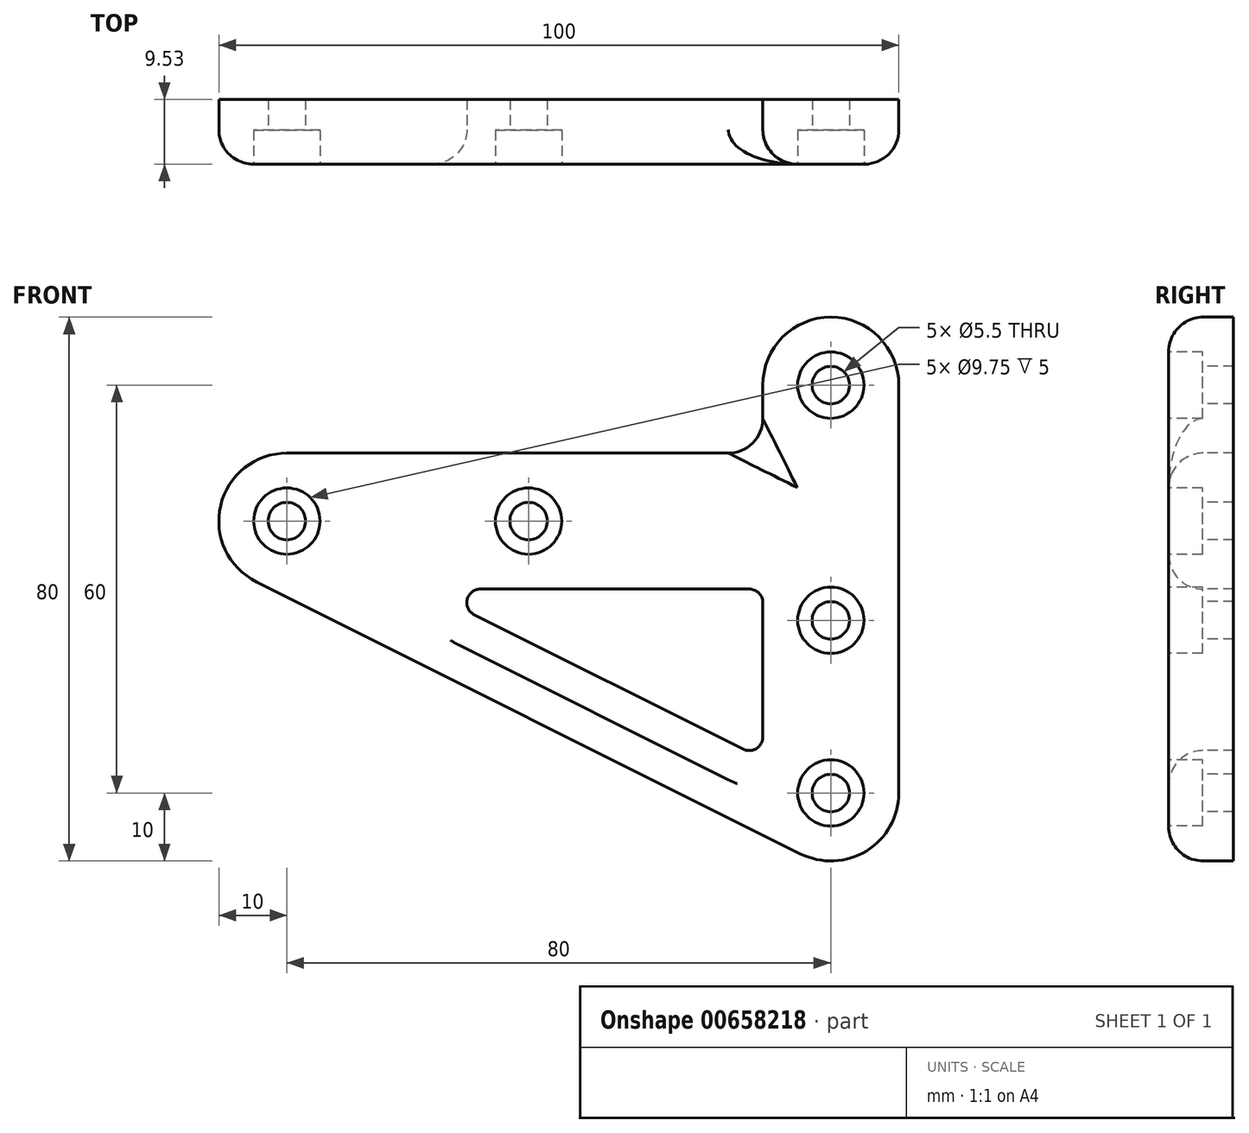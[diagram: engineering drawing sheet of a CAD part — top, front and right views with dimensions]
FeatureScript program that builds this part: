
annotation { "Feature Type Name" : "Feature", "Feature Type Description" : "" }
export const myFeature = defineFeature(function(context is Context, id is Id, definition is map)
    precondition{}
    {
        {
            var Q0;
            Q0=qCreatedBy(makeId("Front.planeOp"),FACE);
            var sketch = newSketch(context, id + "F0", { "sketchPlane" : qUnion([Q0])});
            skPoint(sketch, "E0.MirrorP", {"position": v(-44.45, 0) * mm});
            skPoint(sketch, "E1", {"position": v(0, -40) * mm});
            skArc(sketch, "E2", {"start": v(-4.47, -48.94) * mm, "mid": v(5.26, -48.5) * mm, "end": v(10, -40) * mm});
            skArc(sketch, "E3", {"start": v(-80, 10) * mm, "mid": v(-89.73, 2.3) * mm, "end": v(-84.47, -8.94) * mm});
            skPoint(sketch, "E4", {"position": v(0, 0) * mm});
            skLineSegment(sketch, "E5", {"start": v(-84.47, -8.94) * mm, "end": v(-4.47, -48.94) * mm});
            skLineSegment(sketch, "E6", {"start": v(-80, 10) * mm, "end": v(-10, 10) * mm});
            skLineSegment(sketch, "E7", {"start": v(10, -40) * mm, "end": v(10, 0) * mm});
            skLineSegment(sketch, "E8.0", {"start": v(-52.42, -13.79) * mm, "end": v(-12.9, -33.55) * mm});
            skLineSegment(sketch, "E9.0", {"start": v(-10, -31.76) * mm, "end": v(-10, -12) * mm});
            skLineSegment(sketch, "E10.0", {"start": v(-51.53, -10) * mm, "end": v(-12, -10) * mm});
            skPoint(sketch, "E11.visualSharp", {"position": v(-60, -10) * mm});
            skArc(sketch, "E11.filletArc", {"start": v(-51.53, -10) * mm, "mid": v(-53.47, -11.54) * mm, "end": v(-52.42, -13.79) * mm});
            skPoint(sketch, "E12.visualSharp", {"position": v(-10, -10) * mm});
            skArc(sketch, "E12.filletArc", {"start": v(-10, -12) * mm, "mid": v(-10.59, -10.59) * mm, "end": v(-12, -10) * mm});
            skPoint(sketch, "E13.visualSharp", {"position": v(-10, -35) * mm});
            skArc(sketch, "E13.filletArc", {"start": v(-12.9, -33.55) * mm, "mid": v(-10.95, -33.47) * mm, "end": v(-10, -31.76) * mm});
            skPoint(sketch, "E14", {"position": v(0, 20) * mm});
            skArc(sketch, "E15", {"start": v(10, 20) * mm, "mid": v(0, 30) * mm, "end": v(-10, 20) * mm});
            skLineSegment(sketch, "E16", {"start": v(10, 0) * mm, "end": v(10, 20) * mm});
            skLineSegment(sketch, "E17", {"start": v(-10, 20) * mm, "end": v(-10, 10) * mm});
            skPoint(sketch, "E18", {"position": v(0, -14.6) * mm});
            skSolve(sketch);
        }
        {
            var Q0;
            Q0 = qSketchRegion(id + "F0", true);
            extrude(context, id + "F1", {"entities" : qUnion([Q0]), "oppositeDirection" : true, "depth" : 9.52 * mm, "offsetDistance" : 25.4 * mm});
        }
        {
            var Q0;
            Q0=sQuery(id+"F0.wireOp",VERTEX,"zsvrEA9L-wWyx-hmEm-44rT-VdmW2u0hRzRj.center");
            var Q1;
            Q1=sQuery(id+"F0.wireOp",VERTEX,"E1");
            var Q2;
            Q2=sQuery(id+"F0.wireOp",VERTEX,"E0.MirrorP");
            var Q3;
            Q3=sQuery(id+"F0.wireOp",VERTEX,"E3.center");
            var Q4;
            Q4=sQuery(id+"F0.wireOp",VERTEX,"E18");
            var Q5;
            Q5=sQuery(id+"F0.wireOp",VERTEX,"E14");
            var Q6;
            Q6=makeQuery(id+"F1.opExtrude","SWEPT_BODY",BODY,{"disambiguationData":[OSD([sQuery(id+"F0.wireOp",EDGE,"bf2f238d-4e1d-4e86-ab75-1465cd813df2.MirrorCS"),sQuery(id+"F0.wireOp",EDGE,"7d5bedbb-471c-4160-8e68-eb1f4d767648.MirrorCS"),sQuery(id+"F0.wireOp",EDGE,"bc7fee83-9e46-4c51-805a-8ae9689402aa.MirrorCS"),sQuery(id+"F0.wireOp",EDGE,"e5d497b7-cccf-4703-a1dc-18e520bbeae9.MirrorCS"),sQuery(id+"F0.wireOp",EDGE,"c155fd9a-5cc5-4759-a1c6-071fd15af197.MirrorCS"),sQuery(id+"F0.wireOp",EDGE,"33a989d6-5cc4-4172-ab73-ca817da9f412.MirrorCS"),sQuery(id+"F0.wireOp",EDGE,"1c3aec17-fec7-453e-8acd-3df81b9bc4e3.MirrorCS"),sQuery(id+"F0.wireOp",EDGE,"0cd19f4d-6d86-4b4a-a093-bb589b475590.MirrorCS"),sQuery(id+"F0.wireOp",EDGE,"eee5d6f5-912f-4719-99ba-1d72e724f1e9.MirrorCS"),sQuery(id+"F0.wireOp",EDGE,"64a401ff-d109-42b1-96b9-6f7f2e519c4d.MirrorCS"),sQuery(id+"F0.wireOp",EDGE,"2bc110f3-ae92-45de-b2b7-7df43831b8ab"),sQuery(id+"F0.wireOp",EDGE,"pibmvETk-c1Xj-BIgN-8uma-1jo4IxxjolSW")])]});
            var Q7;
            Q7=makeQuery(id+"F1.opExtrude","SWEPT_BODY",BODY,{"disambiguationData":[OSD([sQuery(id+"F0.wireOp",EDGE,"zsvrEA9L-wWyx-hmEm-44rT-VdmW2u0hRzRj"),sQuery(id+"F0.wireOp",EDGE,"E2"),sQuery(id+"F0.wireOp",EDGE,"E3"),sQuery(id+"F0.wireOp",EDGE,"E5"),sQuery(id+"F0.wireOp",EDGE,"E6"),sQuery(id+"F0.wireOp",EDGE,"E7"),sQuery(id+"F0.wireOp",EDGE,"E8.0"),sQuery(id+"F0.wireOp",EDGE,"E9.0"),sQuery(id+"F0.wireOp",EDGE,"E10.0"),sQuery(id+"F0.wireOp",EDGE,"E11.filletArc"),sQuery(id+"F0.wireOp",EDGE,"E12.filletArc"),sQuery(id+"F0.wireOp",EDGE,"E13.filletArc")])]});
            hole(context, id + "F2", {"style" : HoleStyle.C_BORE, "endStyle" : HoleEndStyle.THROUGH, "standardTappedOrClearance" : lookupTablePath({ "standard" : "ISO", "fit" : "Normal", "size" : "M5", "type" : "Clearance" }), "standardBlindInLast" : lookupTablePath({ "fit" : "Standard", "standard" : "ISO", "size" : "M5", "type" : "Clearance" }), "holeDiameter" : 5.5 * mm, "cBoreDiameter" : 9.75 * mm, "cBoreDepth" : 5 * mm, "majorDiameter" : 6.35 * mm, "isTappedThrough" : true, "tappedDepth" : 12.7 * mm, "tapClearance" : 3, "locations" : qUnion([Q0, Q1, Q2, Q3, Q4, Q5]), "scope" : qUnion([Q6, Q7])});
        }
        {
            var Q0;
            Q0=makeQuery(id+"F1.opExtrude","CAP_EDGE",EDGE,{"disambiguationData":[OSD([sQuery(id+"F0.wireOp",EDGE,"E6")])],"isStart":true});
            var Q1;
            Q1=makeQuery(id+"F1.opExtrude","CAP_EDGE",EDGE,{"disambiguationData":[OSD([sQuery(id+"F0.wireOp",EDGE,"E10.0")])],"isStart":true});
            fillet(context, id + "F3", {"entities" : qUnion([Q0, Q1]), "radius" : 5.08 * mm, "tangentPropagation" : true, "allowEdgeOverflow" : false});
        }
        {
            var Q0;
            Q0=makeQuery(id+"F1.opExtrude","SWEPT_EDGE",EDGE,{"disambiguationData":[OSD([sQuery(id+"F0.wireOp",EDGE,"E6"),sQuery(id+"F0.wireOp",EDGE,"E17")])]});
            fillet(context, id + "F4", {"entities" : qUnion([Q0]), "radius" : 5.08 * mm, "tangentPropagation" : true, "allowEdgeOverflow" : false});
        }
    });
